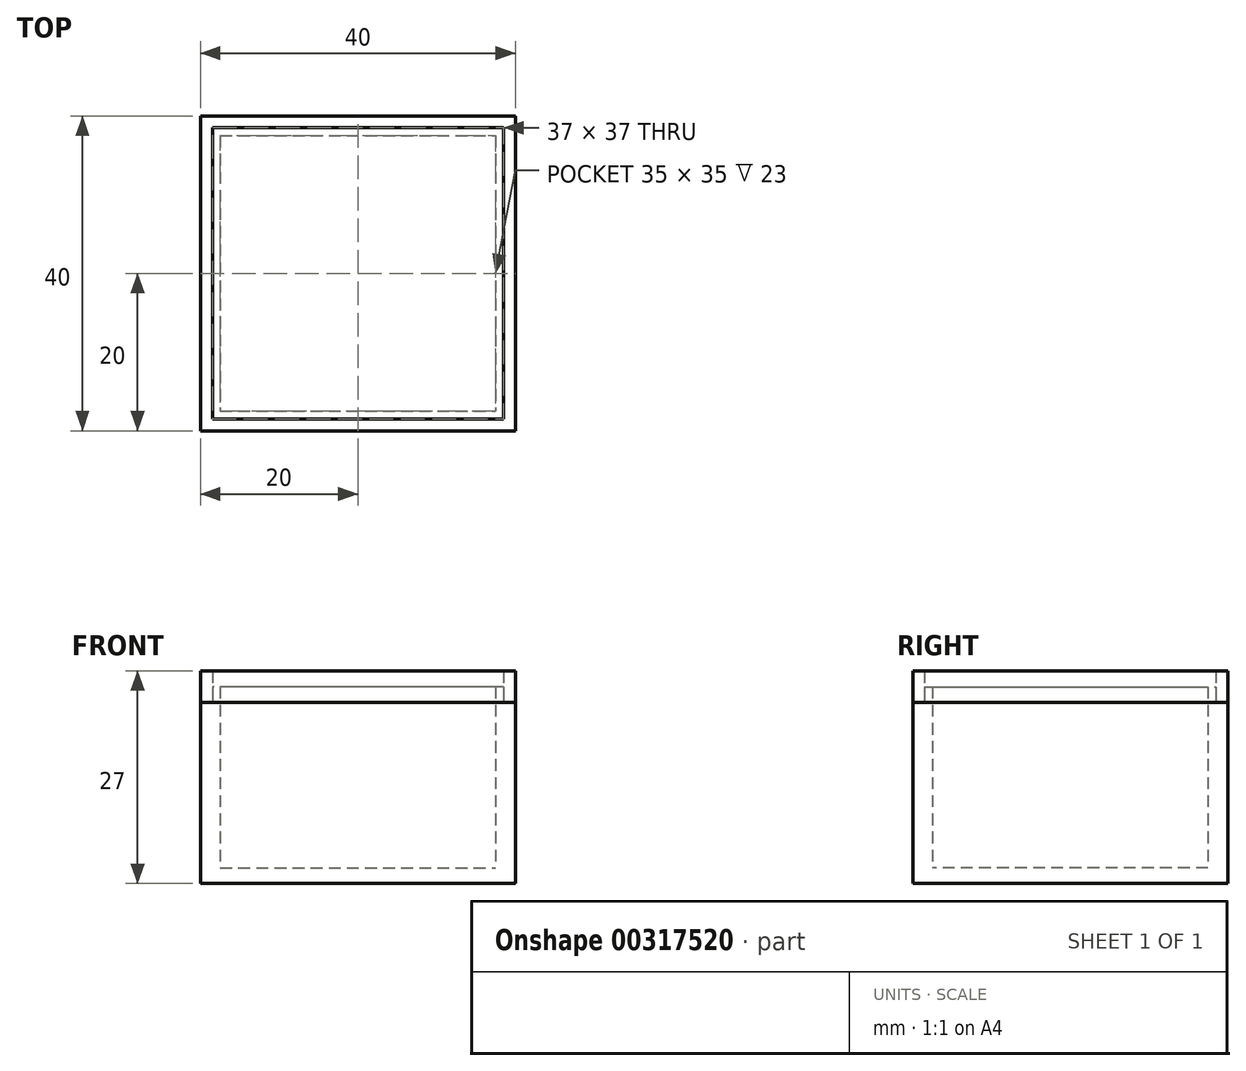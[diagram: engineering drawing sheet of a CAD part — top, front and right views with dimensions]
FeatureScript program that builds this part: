
annotation { "Feature Type Name" : "Feature", "Feature Type Description" : "" }
export const myFeature = defineFeature(function(context is Context, id is Id, definition is map)
    precondition{}
    {
        {
            var Q0;
            Q0=qCreatedBy(makeId("Top.planeOp"),FACE);
            var sketch = newSketch(context, id + "F0", { "sketchPlane" : qUnion([Q0])});
            skLineSegment(sketch, "E0.bottom", {"start": v(20, -20) * mm, "end": v(-20, -20) * mm});
            skLineSegment(sketch, "E0.top", {"start": v(20, 20) * mm, "end": v(-20, 20) * mm});
            skLineSegment(sketch, "E0.left", {"start": v(20, -20) * mm, "end": v(20, 20) * mm});
            skLineSegment(sketch, "E0.right", {"start": v(-20, -20) * mm, "end": v(-20, 20) * mm});
            skPoint(sketch, "E0.middle", {"position": v(0, 0) * mm});
            skLineSegment(sketch, "E1.bottom", {"start": v(18.5, -18.5) * mm, "end": v(-18.5, -18.5) * mm});
            skLineSegment(sketch, "E1.top", {"start": v(18.5, 18.5) * mm, "end": v(-18.5, 18.5) * mm});
            skLineSegment(sketch, "E1.left", {"start": v(18.5, -18.5) * mm, "end": v(18.5, 18.5) * mm});
            skLineSegment(sketch, "E1.right", {"start": v(-18.5, -18.5) * mm, "end": v(-18.5, 18.5) * mm});
            skLineSegment(sketch, "E2.bottom", {"start": v(17, -17) * mm, "end": v(-17, -17) * mm});
            skLineSegment(sketch, "E2.top", {"start": v(17, 17) * mm, "end": v(-17, 17) * mm});
            skLineSegment(sketch, "E2.left", {"start": v(17, -17) * mm, "end": v(17, 17) * mm});
            skLineSegment(sketch, "E2.right", {"start": v(-17, -17) * mm, "end": v(-17, 17) * mm});
            skLineSegment(sketch, "E3.bottom", {"start": v(17.5, -17.5) * mm, "end": v(-17.5, -17.5) * mm});
            skLineSegment(sketch, "E3.top", {"start": v(17.5, 17.5) * mm, "end": v(-17.5, 17.5) * mm});
            skLineSegment(sketch, "E3.left", {"start": v(17.5, -17.5) * mm, "end": v(17.5, 17.5) * mm});
            skLineSegment(sketch, "E3.right", {"start": v(-17.5, -17.5) * mm, "end": v(-17.5, 17.5) * mm});
            skSolve(sketch);
        }
        {
            var Q0;
            Q0=makeQuery(id+"F0.imprint","IMPRINT",FACE,{"disambiguationData":[TD([[makeQuery(id+"F0.imprint","IMPRINT",EDGE,{"derivedFrom":sQuery(id+"F0.wireOp",EDGE,"E0.bottom")}),-1.0]])]});
            var Q1;
            Q1=makeQuery(id+"F0.imprint","IMPRINT",FACE,{"disambiguationData":[TD([[makeQuery(id+"F0.imprint","IMPRINT",EDGE,{"derivedFrom":sQuery(id+"F0.wireOp",EDGE,"E1.bottom")}),-1.0]])]});
            var Q2;
            Q2=makeQuery(id+"F0.imprint","IMPRINT",FACE,{"disambiguationData":[TD([[makeQuery(id+"F0.imprint","IMPRINT",EDGE,{"derivedFrom":sQuery(id+"F0.wireOp",EDGE,"E2.bottom")}),-1.0]])]});
            var Q3;
            Q3=makeQuery(id+"F0.imprint","IMPRINT",FACE,{"disambiguationData":[TD([[makeQuery(id+"F0.imprint","IMPRINT",EDGE,{"derivedFrom":sQuery(id+"F0.wireOp",EDGE,"E2.bottom")}),1.0]])]});
            extrude(context, id + "F1", {"entities" : qUnion([Q0, Q1, Q2, Q3]), "depth" : 2 * mm});
        }
        {
            var Q0;
            Q0=makeQuery(id+"F0.imprint","IMPRINT",FACE,{"disambiguationData":[TD([[makeQuery(id+"F0.imprint","IMPRINT",EDGE,{"derivedFrom":sQuery(id+"F0.wireOp",EDGE,"E1.bottom")}),-1.0]])]});
            extrude(context, id + "F2", {"entities" : qUnion([Q0]), "operationType" : NewBodyOperationType.ADD, "depth" : 25 * mm});
        }
        {
            var Q0;
            Q0=makeQuery(id+"F0.imprint","IMPRINT",FACE,{"disambiguationData":[TD([[makeQuery(id+"F0.imprint","IMPRINT",EDGE,{"derivedFrom":sQuery(id+"F0.wireOp",EDGE,"E0.bottom")}),-1.0]])]});
            extrude(context, id + "F3", {"entities" : qUnion([Q0]), "operationType" : NewBodyOperationType.ADD, "depth" : 23 * mm});
        }
        {
            var Q0;
            Q0=makeQuery(id+"F0.imprint","IMPRINT",FACE,{"disambiguationData":[TD([[makeQuery(id+"F0.imprint","IMPRINT",EDGE,{"derivedFrom":sQuery(id+"F0.wireOp",EDGE,"E0.bottom")}),-1.0]])]});
            extrude(context, id + "F4", {"entities" : qUnion([Q0]), "depth" : 27 * mm, "hasSecondDirection" : true, "secondDirectionOppositeDirection" : false, "secondDirectionDepth" : 23 * mm});
        }
        {
            var Q0;
            Q0=makeQuery(id+"F0.imprint","IMPRINT",FACE,{"disambiguationData":[TD([[makeQuery(id+"F0.imprint","IMPRINT",EDGE,{"derivedFrom":sQuery(id+"F0.wireOp",EDGE,"E2.bottom")}),-1.0]])]});
            var Q1;
            Q1=makeQuery(id+"F0.imprint","IMPRINT",FACE,{"disambiguationData":[TD([[makeQuery(id+"F0.imprint","IMPRINT",EDGE,{"derivedFrom":sQuery(id+"F0.wireOp",EDGE,"E2.bottom")}),1.0]])]});
            var Q2;
            Q2=makeQuery(id+"F0.imprint","IMPRINT",FACE,{"disambiguationData":[TD([[makeQuery(id+"F0.imprint","IMPRINT",EDGE,{"derivedFrom":sQuery(id+"F0.wireOp",EDGE,"E1.bottom")}),-1.0]])]});
            extrude(context, id + "F5", {"entities" : qUnion([Q0, Q1, Q2]), "depth" : 27 * mm, "hasSecondDirection" : true, "secondDirectionOppositeDirection" : false, "secondDirectionDepth" : 25 * mm});
        }
    });
